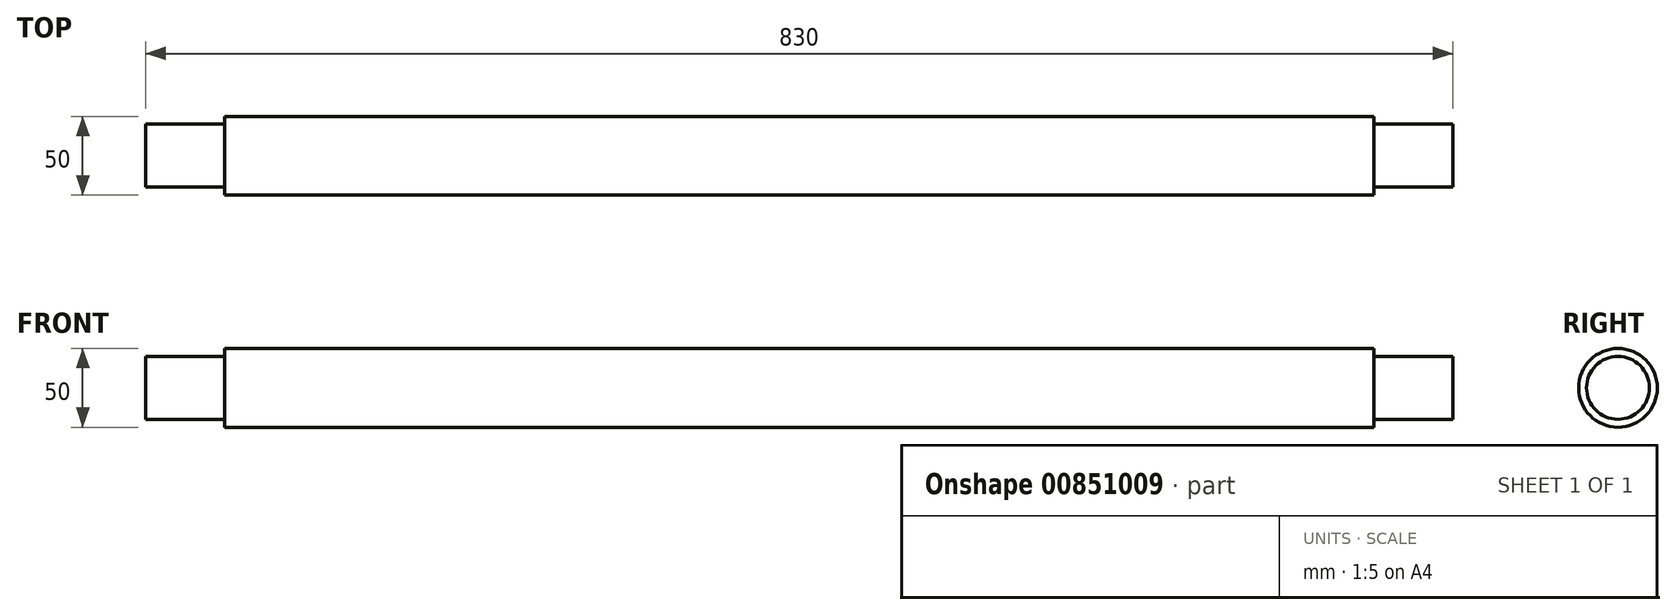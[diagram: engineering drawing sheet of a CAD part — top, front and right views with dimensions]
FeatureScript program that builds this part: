
annotation { "Feature Type Name" : "Feature", "Feature Type Description" : "" }
export const myFeature = defineFeature(function(context is Context, id is Id, definition is map)
    precondition{}
    {
        {
            var Q0;
            Q0=qCreatedBy(makeId("Front.planeOp"),FACE);
            var sketch = newSketch(context, id + "F0", { "sketchPlane" : qUnion([Q0])});
            skLineSegment(sketch, "E0", {"start": v(0, 0) * mm, "end": v(830, 0) * mm});
            skLineSegment(sketch, "E1", {"start": v(830, 0) * mm, "end": v(830, -20) * mm});
            skLineSegment(sketch, "E2", {"start": v(830, -20) * mm, "end": v(780, -20) * mm});
            skLineSegment(sketch, "E3", {"start": v(780, -20) * mm, "end": v(780, -25) * mm});
            skLineSegment(sketch, "E4", {"start": v(780, -25) * mm, "end": v(50, -25) * mm});
            skLineSegment(sketch, "E5", {"start": v(50, -25) * mm, "end": v(50, -20) * mm});
            skLineSegment(sketch, "E6", {"start": v(50, -20) * mm, "end": v(0, -20) * mm});
            skLineSegment(sketch, "E7", {"start": v(0, -20) * mm, "end": v(0, 0) * mm});
            skSolve(sketch);
        }
        {
            var Q0;
            Q0=makeQuery(id+"F0.imprint","IMPRINT",FACE,{"disambiguationData":[TD([[makeQuery(id+"F0.imprint","IMPRINT",EDGE,{"derivedFrom":sQuery(id+"F0.wireOp",EDGE,"E0")}),-1.0]])]});
            var Q1;
            Q1=sQuery(id+"F0.wireOp",EDGE,"E0");
            revolve(context, id + "F1", {"surfaceOperationType" : NewSurfaceOperationType.NEW, "entities" : qUnion([Q0]), "axis" : qUnion([Q1]), "revolveType" : RevolveType.FULL});
        }
    });
